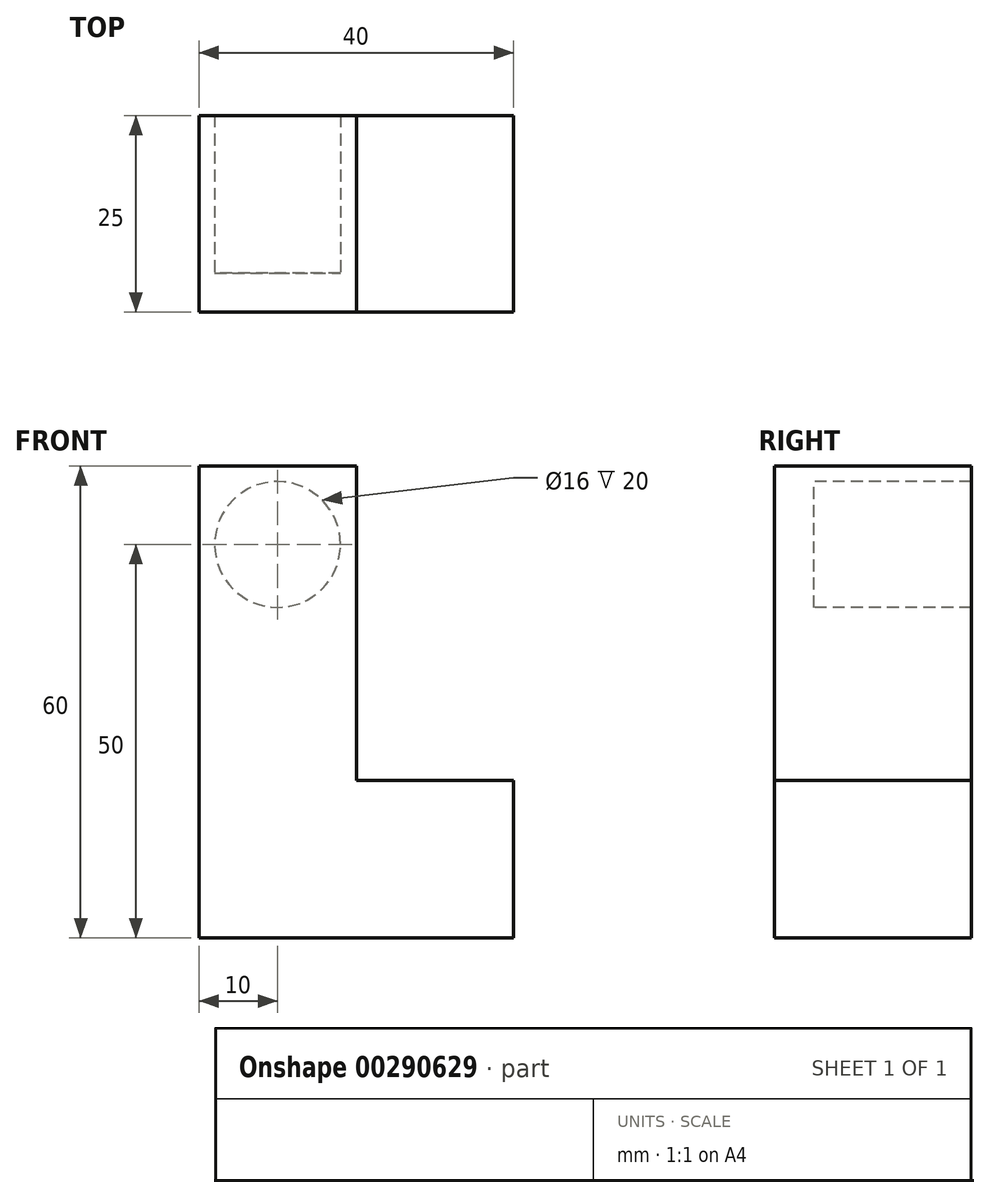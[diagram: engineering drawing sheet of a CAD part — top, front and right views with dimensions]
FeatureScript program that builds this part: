
annotation { "Feature Type Name" : "Feature", "Feature Type Description" : "" }
export const myFeature = defineFeature(function(context is Context, id is Id, definition is map)
    precondition{}
    {
        {
            var Q0;
            Q0=qCreatedBy(makeId("Top.planeOp"),FACE);
            var sketch = newSketch(context, id + "F0", { "sketchPlane" : qUnion([Q0])});
            skLineSegment(sketch, "E0.bottom", {"start": v(-20, 12.5) * mm, "end": v(20, 12.5) * mm});
            skLineSegment(sketch, "E0.top", {"start": v(-20, -12.5) * mm, "end": v(20, -12.5) * mm});
            skLineSegment(sketch, "E0.left", {"start": v(-20, 12.5) * mm, "end": v(-20, -12.5) * mm});
            skLineSegment(sketch, "E0.right", {"start": v(20, 12.5) * mm, "end": v(20, -12.5) * mm});
            skLineSegment(sketch, "E1", {"start": v(0, 12.5) * mm, "end": v(0, -12.5) * mm, "construction": true});
            skLineSegment(sketch, "E2", {"start": v(-20, 0) * mm, "end": v(20, 0) * mm, "construction": true});
            skPoint(sketch, "E2.startSnap0", {"position": v(-20, 0) * mm});
            skLineSegment(sketch, "E3", {"start": v(0, 12.5) * mm, "end": v(0, -12.5) * mm});
            skSolve(sketch);
        }
        {
            var Q0;
            {var subQ0=sQuery(id+"F0.wireOp",EDGE,"E0.left");Q0=makeQuery(id+"F0.imprint","IMPRINT",FACE,{"disambiguationData":[TD([[makeQuery(id+"F0.imprint","IMPRINT",EDGE,{"derivedFrom":subQ0}),1.0]])]});}
            extrude(context, id + "F1", {"entities" : qUnion([Q0]), "depth" : 60 * mm});
        }
        {
            var Q0;
            {var subQ0=sQuery(id+"F0.wireOp",EDGE,"E0.right");Q0=makeQuery(id+"F0.imprint","IMPRINT",FACE,{"disambiguationData":[TD([[makeQuery(id+"F0.imprint","IMPRINT",EDGE,{"derivedFrom":subQ0}),-1.0]])]});}
            extrude(context, id + "F2", {"entities" : qUnion([Q0]), "operationType" : NewBodyOperationType.ADD, "depth" : 20 * mm});
        }
        {
            var Q0;
            {var subQ0=sQuery(id+"F0.wireOp",EDGE,"E0.top");Q0=makeQuery(id+"F2.boolean.opBoolean","MERGE",FACE,{"derivedFrom":[makeQuery(id+"F1.opExtrude","SWEPT_FACE",FACE,{"disambiguationData":[OSD([subQ0])]}),makeQuery(id+"F2.opExtrude","SWEPT_FACE",FACE,{"disambiguationData":[OSD([subQ0])]})]});}
            var sketch = newSketch(context, id + "F3", { "sketchPlane" : qUnion([Q0])});
            skLineSegment(sketch, "E4", {"start": v(-10, 60) * mm, "end": v(-10, 0) * mm, "construction": true});
            skPoint(sketch, "E5.trimOffspring.end.orphan", {"position": v(-20, 30) * mm});
            skPoint(sketch, "E6.center.orphan", {"position": v(-10, 25) * mm});
            skPoint(sketch, "E7.start.orphan", {"position": v(0, 20) * mm});
            skLineSegment(sketch, "E8", {"start": v(-20, 50) * mm, "end": v(0, 50) * mm, "construction": true});
            skCircle(sketch, "E9", {"center": v(-10, 50) * mm, "radius": 8 * mm});
            skSolve(sketch);
        }
        {
            var Q0;
            Q0=makeQuery(id+"F3.imprint","IMPRINT",FACE,{"disambiguationData":[TD([[makeQuery(id+"F3.imprint","IMPRINT",EDGE,{"derivedFrom":sQuery(id+"F3.wireOp",EDGE,"E9")}),1.0]])]});
            extrude(context, id + "F4", {"entities" : qUnion([Q0]), "operationType" : NewBodyOperationType.REMOVE, "oppositeDirection" : true, "depth" : 25 * mm, "hasSecondDirection" : true, "secondDirectionOppositeDirection" : true, "secondDirectionDepth" : 5 * mm});
        }
    });
